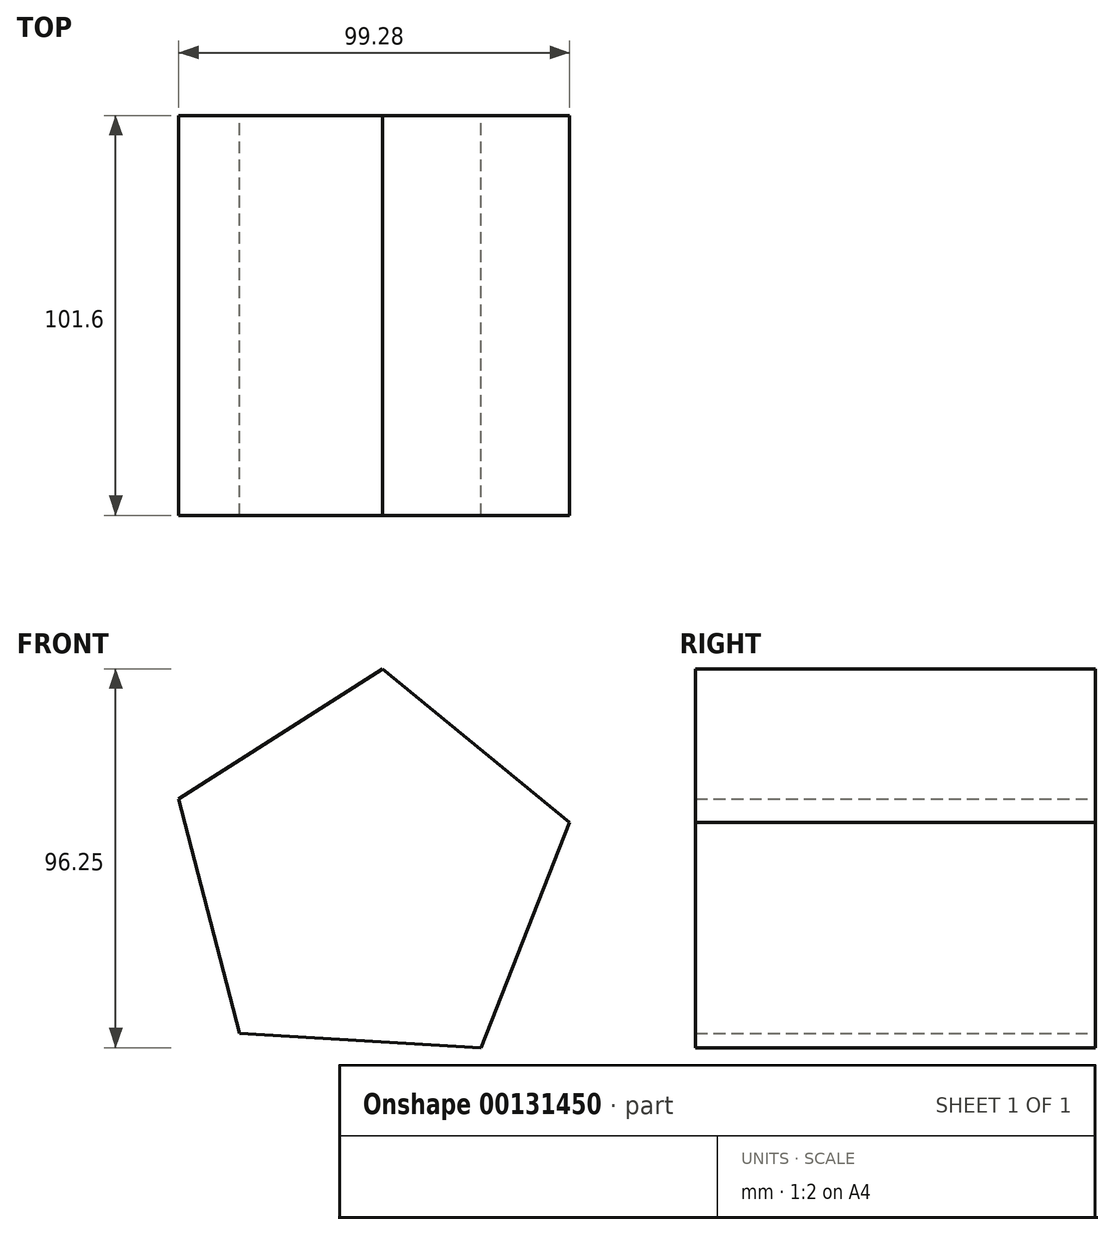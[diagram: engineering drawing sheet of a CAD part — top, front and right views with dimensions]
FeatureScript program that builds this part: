
annotation { "Feature Type Name" : "Feature", "Feature Type Description" : "" }
export const myFeature = defineFeature(function(context is Context, id is Id, definition is map)
    precondition{}
    {
        {
            var Q0;
            Q0=qCreatedBy(makeId("Front.planeOp"),FACE);
            var sketch = newSketch(context, id + "F0", { "sketchPlane" : qUnion([Q0])});
            skCircle(sketch, "E0.cCircle", {"center": v(0, 0) * mm, "radius": 52.29 * mm, "construction": true});
            skLineSegment(sketch, "E0.0", {"start": v(-48.68, 19.1) * mm, "end": v(3.12, 52.2) * mm});
            skLineSegment(sketch, "E0.1", {"start": v(3.12, 52.2) * mm, "end": v(50.6, 13.17) * mm});
            skLineSegment(sketch, "E0.2", {"start": v(50.6, 13.17) * mm, "end": v(28.16, -44.06) * mm});
            skLineSegment(sketch, "E0.3", {"start": v(28.16, -44.06) * mm, "end": v(-33.2, -40.4) * mm});
            skLineSegment(sketch, "E0.4", {"start": v(-33.2, -40.4) * mm, "end": v(-48.68, 19.1) * mm});
            skSolve(sketch);
        }
        {
            var Q0;
            Q0=makeQuery(id+"F0.imprint","IMPRINT",FACE,{"disambiguationData":[TD([[makeQuery(id+"F0.imprint","IMPRINT",EDGE,{"derivedFrom":sQuery(id+"F0.wireOp",EDGE,"E0.0")}),-1.0]])]});
            extrude(context, id + "F1", {"entities" : qUnion([Q0]), "depth" : 101.6 * mm});
        }
    });
